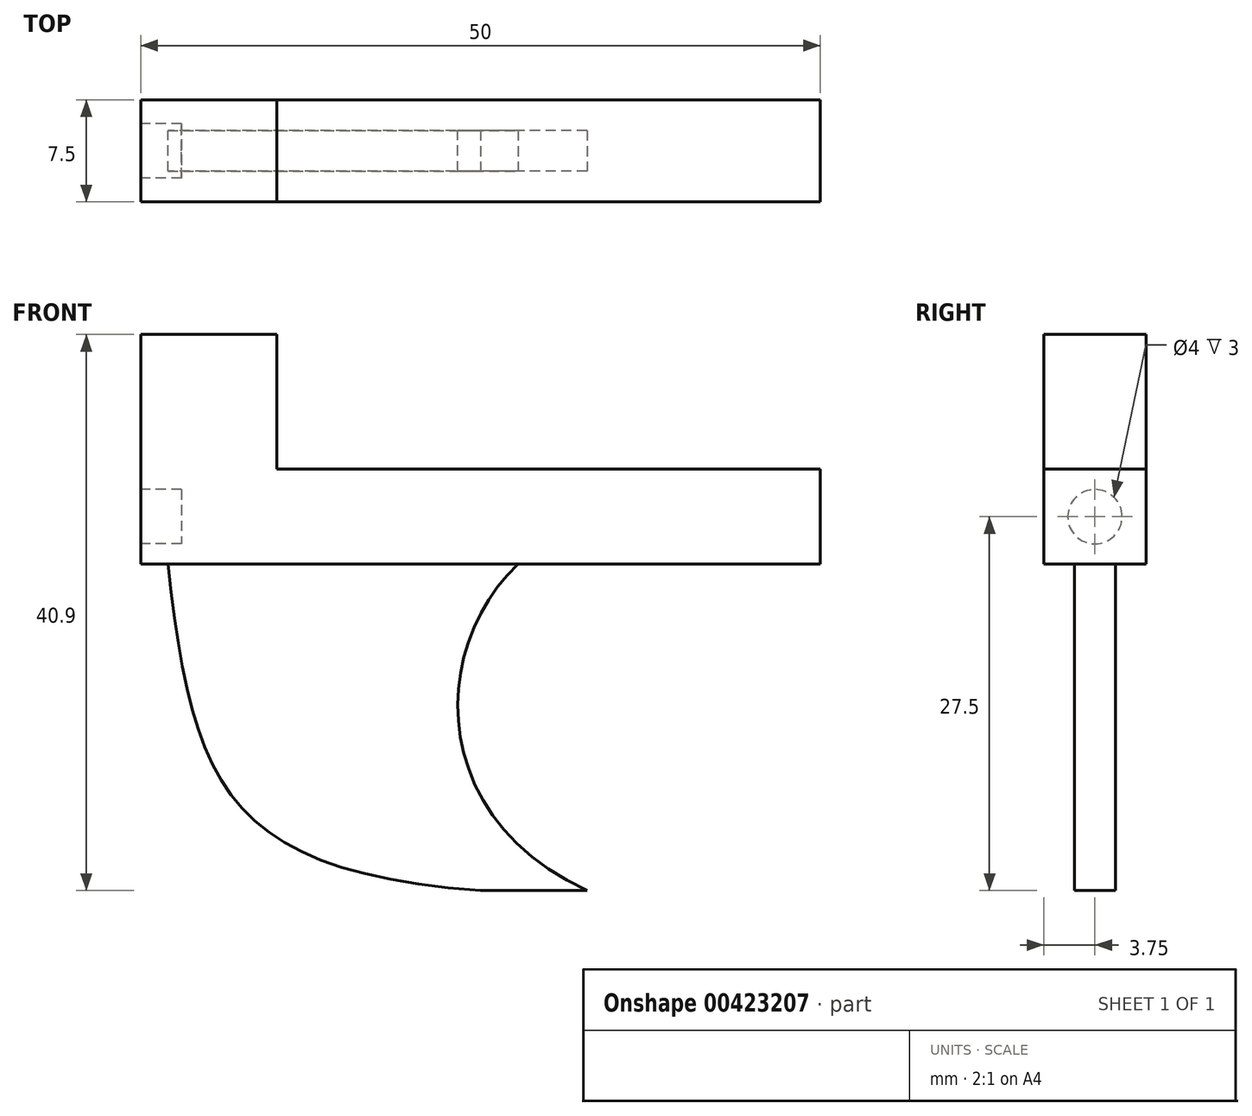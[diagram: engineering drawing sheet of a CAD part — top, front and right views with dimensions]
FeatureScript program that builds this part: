
annotation { "Feature Type Name" : "Feature", "Feature Type Description" : "" }
export const myFeature = defineFeature(function(context is Context, id is Id, definition is map)
    precondition{}
    {
        {
            var Q0;
            Q0=qCreatedBy(makeId("Top.planeOp"),FACE);
            var sketch = newSketch(context, id + "F0", { "sketchPlane" : qUnion([Q0])});
            skLineSegment(sketch, "E0.bottom", {"start": v(-25, 3.75) * mm, "end": v(25, 3.75) * mm});
            skLineSegment(sketch, "E0.top", {"start": v(-25, -3.75) * mm, "end": v(25, -3.75) * mm});
            skLineSegment(sketch, "E0.left", {"start": v(-25, 3.75) * mm, "end": v(-25, -3.75) * mm});
            skLineSegment(sketch, "E0.right", {"start": v(25, 3.75) * mm, "end": v(25, -3.75) * mm});
            skPoint(sketch, "E0.middle", {"position": v(0, 0) * mm});
            skSolve(sketch);
        }
        {
            var Q0;
            Q0 = qSketchRegion(id + "F0", true);
            extrude(context, id + "F1", {"entities" : qUnion([Q0]), "depth" : 7 * mm, "offsetDistance" : 25 * mm});
        }
        {
            var Q0;
            Q0=makeQuery(id+"F1.opExtrude","CAP_FACE",FACE,{"disambiguationData":[OSD([sQuery(id+"F0.wireOp",EDGE,"E0.bottom"),sQuery(id+"F0.wireOp",EDGE,"E0.top"),sQuery(id+"F0.wireOp",EDGE,"E0.left"),sQuery(id+"F0.wireOp",EDGE,"E0.right")])],"isStart":true});
            var sketch = newSketch(context, id + "F2", { "sketchPlane" : qUnion([Q0])});
            skLineSegment(sketch, "E1", {"start": v(25, 3.75) * mm, "end": v(15, 3.75) * mm});
            skLineSegment(sketch, "E2.bottom", {"start": v(15, 3.75) * mm, "end": v(-20, 3.75) * mm});
            skLineSegment(sketch, "E2.top", {"start": v(15, -3.75) * mm, "end": v(-20, -3.75) * mm});
            skLineSegment(sketch, "E3", {"start": v(15, -3.75) * mm, "end": v(15, -1.5) * mm});
            skLineSegment(sketch, "E4", {"start": v(15, 3.75) * mm, "end": v(15, 1.5) * mm});
            skLineSegment(sketch, "E5", {"start": v(15, 1.5) * mm, "end": v(15, -1.5) * mm});
            skLineSegment(sketch, "E6.bottom", {"start": v(15, 1.5) * mm, "end": v(-23, 1.5) * mm});
            skLineSegment(sketch, "E6.top", {"start": v(15, -1.5) * mm, "end": v(-23, -1.5) * mm});
            skLineSegment(sketch, "E6.right", {"start": v(-23, 1.5) * mm, "end": v(-23, -1.5) * mm});
            skSolve(sketch);
        }
        {
            var Q0;
            Q0 = qSketchRegion(id + "F2", true);
            extrude(context, id + "F3", {"entities" : qUnion([Q0]), "operationType" : NewBodyOperationType.ADD, "depth" : 24 * mm, "offsetDistance" : 25 * mm});
        }
        {
            var Q0;
            Q0=makeQuery(id+"F3.opExtrude","SWEPT_FACE",FACE,{"disambiguationData":[OSD([sQuery(id+"F2.wireOp",EDGE,"E6.bottom")])]});
            var sketch = newSketch(context, id + "F4", { "sketchPlane" : qUnion([Q0])});
            skPoint(sketch, "E7.1.internal.snap0", {"position": v(-4, -24) * mm});
            skFitSpline(sketch, "E7", {"points": [v(-23, 0) * mm, v(0, -24) * mm], "startDerivative": vector(5.43, -48) * mm, "endDerivative": vector(57.06, -4.3) * mm});
            skFitSpline(sketch, "E8", {"points": [v(7.83, -24) * mm, v(2.76, 0) * mm], "startDerivative": vector(-35.97, 16.7) * mm, "endDerivative": vector(18.97, 17.67) * mm});
            skSolve(sketch);
        }
        {
            var Q0;
            {var subQ0=sQuery(id+"F4.wireOp",EDGE,"E7");Q0=makeQuery(id+"F4.imprint","IMPRINT",FACE,{"disambiguationData":[TD([[makeQuery(id+"F4.imprint","IMPRINT",EDGE,{"derivedFrom":subQ0}),-1.0]])]});}
            var Q1;
            {var subQ0=sQuery(id+"F4.wireOp",EDGE,"E8");Q1=makeQuery(id+"F4.imprint","IMPRINT",FACE,{"disambiguationData":[TD([[makeQuery(id+"F4.imprint","IMPRINT",EDGE,{"derivedFrom":subQ0}),-1.0]])]});}
            extrude(context, id + "F5", {"entities" : qUnion([Q0, Q1]), "operationType" : NewBodyOperationType.REMOVE, "oppositeDirection" : true, "depth" : 25 * mm, "offsetDistance" : 25 * mm});
        }
        {
            var Q0;
            Q0=makeQuery(id+"F1.opExtrude","SWEPT_FACE",FACE,{"disambiguationData":[OSD([sQuery(id+"F0.wireOp",EDGE,"E0.left")])]});
            var sketch = newSketch(context, id + "F6", { "sketchPlane" : qUnion([Q0])});
            skCircle(sketch, "E9", {"center": v(0, 3.5) * mm, "radius": 2 * mm});
            skPoint(sketch, "E9.centerSnap0", {"position": v(0, 7) * mm});
            skPoint(sketch, "E9.centerSnap1", {"position": v(-3.75, 3.5) * mm});
            skSolve(sketch);
        }
        {
            var Q0;
            Q0 = qSketchRegion(id + "F6", true);
            extrude(context, id + "F7", {"entities" : qUnion([Q0]), "operationType" : NewBodyOperationType.REMOVE, "oppositeDirection" : true, "depth" : 3 * mm, "offsetDistance" : 25 * mm});
        }
        {
            var Q0;
            Q0=makeQuery(id+"F1.opExtrude","CAP_FACE",FACE,{"disambiguationData":[OSD([sQuery(id+"F0.wireOp",EDGE,"E0.bottom"),sQuery(id+"F0.wireOp",EDGE,"E0.top"),sQuery(id+"F0.wireOp",EDGE,"E0.left"),sQuery(id+"F0.wireOp",EDGE,"E0.right")])],"isStart":false});
            var sketch = newSketch(context, id + "F8", { "sketchPlane" : qUnion([Q0])});
            skLineSegment(sketch, "E10.bottom", {"start": v(-25, 3.75) * mm, "end": v(-15, 3.75) * mm});
            skLineSegment(sketch, "E10.top", {"start": v(-25, -3.75) * mm, "end": v(-15, -3.75) * mm});
            skLineSegment(sketch, "E10.left", {"start": v(-25, 3.75) * mm, "end": v(-25, -3.75) * mm});
            skLineSegment(sketch, "E10.right", {"start": v(-15, 3.75) * mm, "end": v(-15, -3.75) * mm});
            skSolve(sketch);
        }
        {
            var Q0;
            Q0=makeQuery(id+"F8.imprint","IMPRINT",FACE,{"disambiguationData":[TD([[makeQuery(id+"F8.imprint","IMPRINT",EDGE,{"derivedFrom":sQuery(id+"F8.wireOp",EDGE,"E10.bottom")}),-1.0]])]});
            extrude(context, id + "F9", {"entities" : qUnion([Q0]), "operationType" : NewBodyOperationType.ADD, "depth" : 9.9 * mm, "offsetDistance" : 25 * mm});
        }
    });
